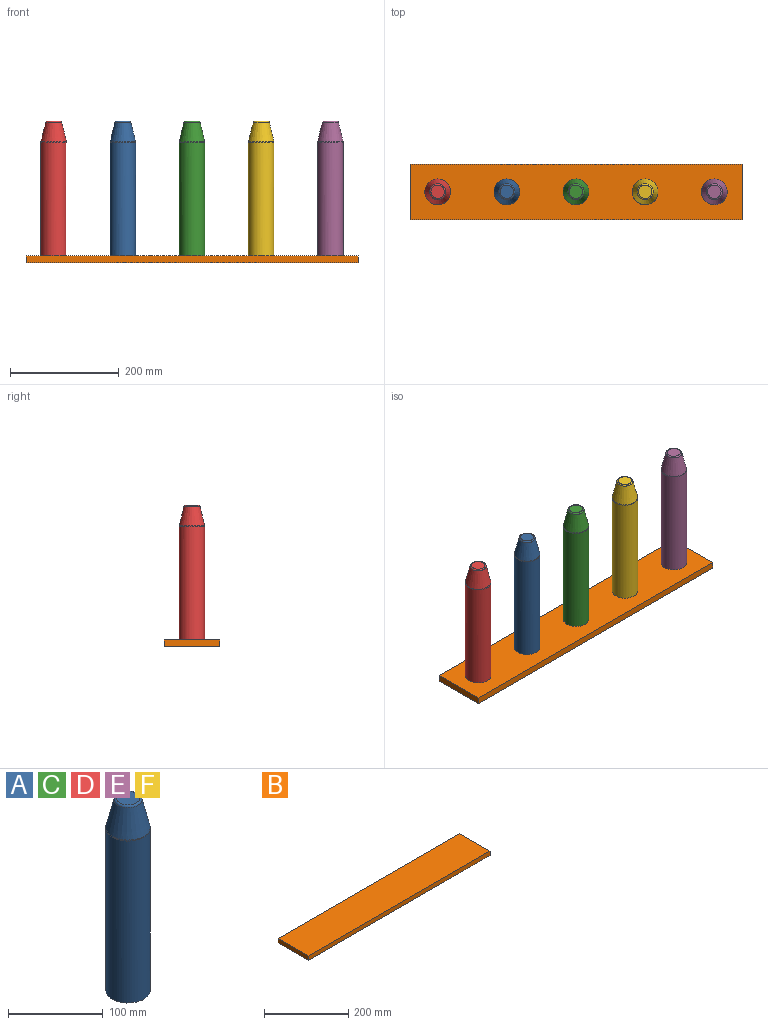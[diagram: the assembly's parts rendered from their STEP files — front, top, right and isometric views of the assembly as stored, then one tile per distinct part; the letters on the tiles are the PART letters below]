
ASSEMBLY  parts=6 mates=1
PART A: 6 faces, bbox 50.9x50.9x247.7 mm
  f0: plane 24.58x24.58mm, normal (0,0,1), area 474.4mm2, adj f4
  f1: plane 46.99x46.99mm, normal (0,0,-1), area 1734.2mm2, adj f2
  f2: cylinder r=23.49mm len=208.95mm, axis (0,0,-1), area 30845.2mm2, adj f1,f5
  f3: cone r=23.49mm half-angle=13.6deg, axis (0,0,-1), area 4381.1mm2, adj f4,f5
  f4: torus R=12.29mm, axis (0,0,1), area 292.6mm2, adj f0,f3
  f5: torus R=18.41mm, axis (0,0,1), area 177.5mm2, adj f2,f3
PART B: 6 faces, bbox 609.6x101.6x12.7 mm
  f0: plane 101.6x12.7mm, normal (-1,0,0), area 1290.3mm2, adj f1,f3,f4,f5
  f1: plane 609.6x12.7mm, normal (0,-1,0), area 7741.9mm2, adj f0,f2,f4,f5
  f2: plane 101.6x12.7mm, normal (1,0,0), area 1290.3mm2, adj f1,f3,f4,f5
  f3: plane 609.6x12.7mm, normal (0,1,0), area 7741.9mm2, adj f0,f2,f4,f5
  f4: plane 609.6x101.6mm, normal (0,0,1), area 61935.4mm2, adj f0,f1,f2,f3
  f5: plane 609.6x101.6mm, normal (0,0,-1), area 61935.4mm2, adj f0,f1,f2,f3
PART C: same geometry as A
PART D: same geometry as A
PART E: same geometry as A
PART F: same geometry as A
PLACE A t=(-127,0,12.7)mm
PLACE B at identity
PLACE C t=(0,0,12.7)mm
PLACE D t=(-254,0,12.7)mm
PLACE E t=(254,0,12.7)mm
PLACE F t=(127,0,12.7)mm
MATE fastened D.f2 <-> B.f4  axis (0,0,-1) through (-254,0,12.7)mm
